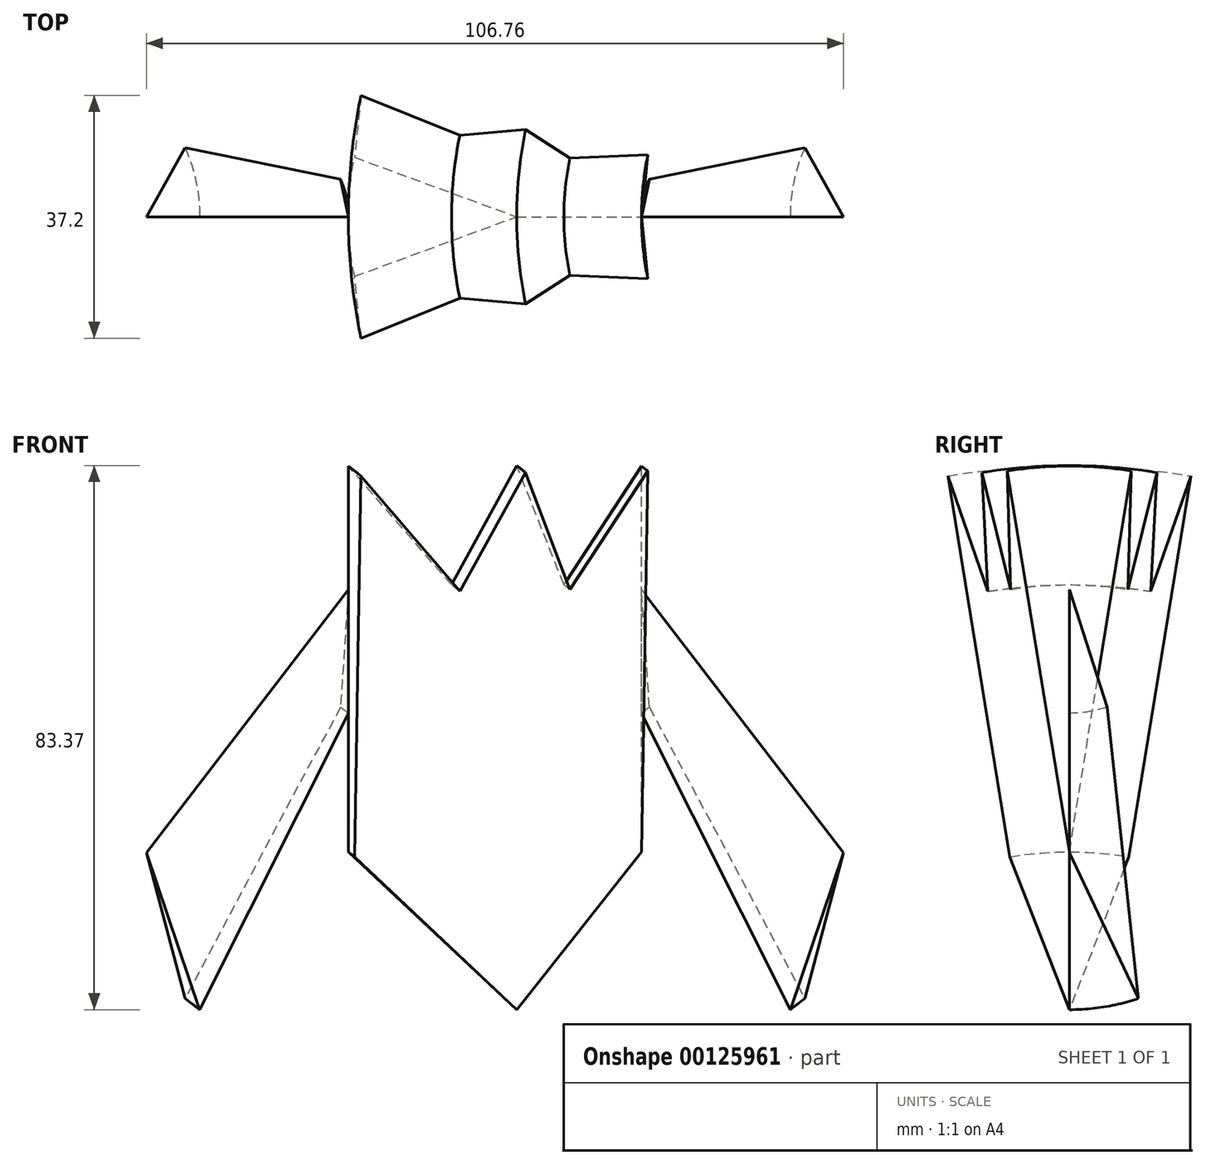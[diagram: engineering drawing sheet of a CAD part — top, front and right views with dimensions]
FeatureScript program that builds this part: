
annotation { "Feature Type Name" : "Feature", "Feature Type Description" : "" }
export const myFeature = defineFeature(function(context is Context, id is Id, definition is map)
    precondition{}
    {
        {
            var Q0;
            Q0=qCreatedBy(makeId("Front.planeOp"),FACE);
            var sketch = newSketch(context, id + "F0", { "sketchPlane" : qUnion([Q0])});
            skLineSegment(sketch, "E0", {"start": v(0, 0) * mm, "end": v(19.12, 24.18) * mm});
            skLineSegment(sketch, "E1", {"start": v(19.12, 24.18) * mm, "end": v(19.12, 45.4) * mm});
            skLineSegment(sketch, "E2", {"start": v(19.12, 45.4) * mm, "end": v(19.12, 83.29) * mm});
            skLineSegment(sketch, "E3", {"start": v(19.12, 83.29) * mm, "end": v(7.25, 65.1) * mm});
            skLineSegment(sketch, "E4", {"start": v(7.25, 65.1) * mm, "end": v(0, 83.37) * mm});
            skLineSegment(sketch, "E5", {"start": v(0, 83.37) * mm, "end": v(-9.98, 65.1) * mm});
            skLineSegment(sketch, "E6", {"start": v(-9.98, 65.1) * mm, "end": v(-25.76, 83.29) * mm});
            skLineSegment(sketch, "E7", {"start": v(-25.76, 83.29) * mm, "end": v(-25.76, 45.4) * mm});
            skLineSegment(sketch, "E8", {"start": v(-25.76, 45.4) * mm, "end": v(-25.76, 24.18) * mm});
            skLineSegment(sketch, "E9", {"start": v(-25.76, 24.18) * mm, "end": v(0, 0) * mm});
            skLineSegment(sketch, "E10", {"start": v(-25.76, 45.4) * mm, "end": v(-48.54, 0) * mm});
            skLineSegment(sketch, "E11", {"start": v(-48.54, 0) * mm, "end": v(-56.7, 24.05) * mm});
            skLineSegment(sketch, "E12", {"start": v(-56.7, 24.05) * mm, "end": v(-25.76, 64.35) * mm});
            skLineSegment(sketch, "E13", {"start": v(19.12, 64.35) * mm, "end": v(50.06, 24.05) * mm});
            skLineSegment(sketch, "E14", {"start": v(19.12, 45.4) * mm, "end": v(41.9, 0) * mm});
            skLineSegment(sketch, "E15", {"start": v(41.9, 0) * mm, "end": v(50.06, 24.05) * mm});
            skSolve(sketch);
        }
        {
            var Q0;
            Q0=makeQuery(id+"F0.imprint","IMPRINT",FACE,{"disambiguationData":[TD([[makeQuery(id+"F0.imprint","IMPRINT",EDGE,{"derivedFrom":sQuery(id+"F0.wireOp",EDGE,"E0")}),1.0]])]});
            var Q1;
            Q1=sQuery(id+"F0.wireOp",EDGE,"E0");
            revolve(context, id + "F1", {"entities" : qUnion([Q0]), "axis" : qUnion([Q1]), "revolveType" : RevolveType.SYMMETRIC, "angle" : 30 * degree});
        }
        {
            var Q0;
            {var subQ2=sQuery(id+"F0.wireOp",EDGE,"E13");Q0=makeQuery(id+"F0.imprint","IMPRINT",FACE,{"disambiguationData":[TD([[makeQuery(id+"F0.imprint","IMPRINT",EDGE,{"derivedFrom":subQ2}),-1.0]])]});}
            var Q1;
            Q1=sQuery(id+"F0.wireOp",EDGE,"E13");
            revolve(context, id + "F2", {"entities" : qUnion([Q0]), "axis" : qUnion([Q1]), "revolveType" : RevolveType.ONE_DIRECTION, "angle" : 30 * degree});
        }
        {
            var Q0;
            {var subQ0=sQuery(id+"F0.wireOp",EDGE,"E10");Q0=makeQuery(id+"F0.imprint","IMPRINT",FACE,{"disambiguationData":[TD([[makeQuery(id+"F0.imprint","IMPRINT",EDGE,{"derivedFrom":subQ0}),-1.0]])]});}
            var Q1;
            Q1=sQuery(id+"F0.wireOp",EDGE,"E12");
            revolve(context, id + "F3", {"entities" : qUnion([Q0]), "axis" : qUnion([Q1]), "revolveType" : RevolveType.ONE_DIRECTION, "angle" : 30 * degree});
        }
    });
